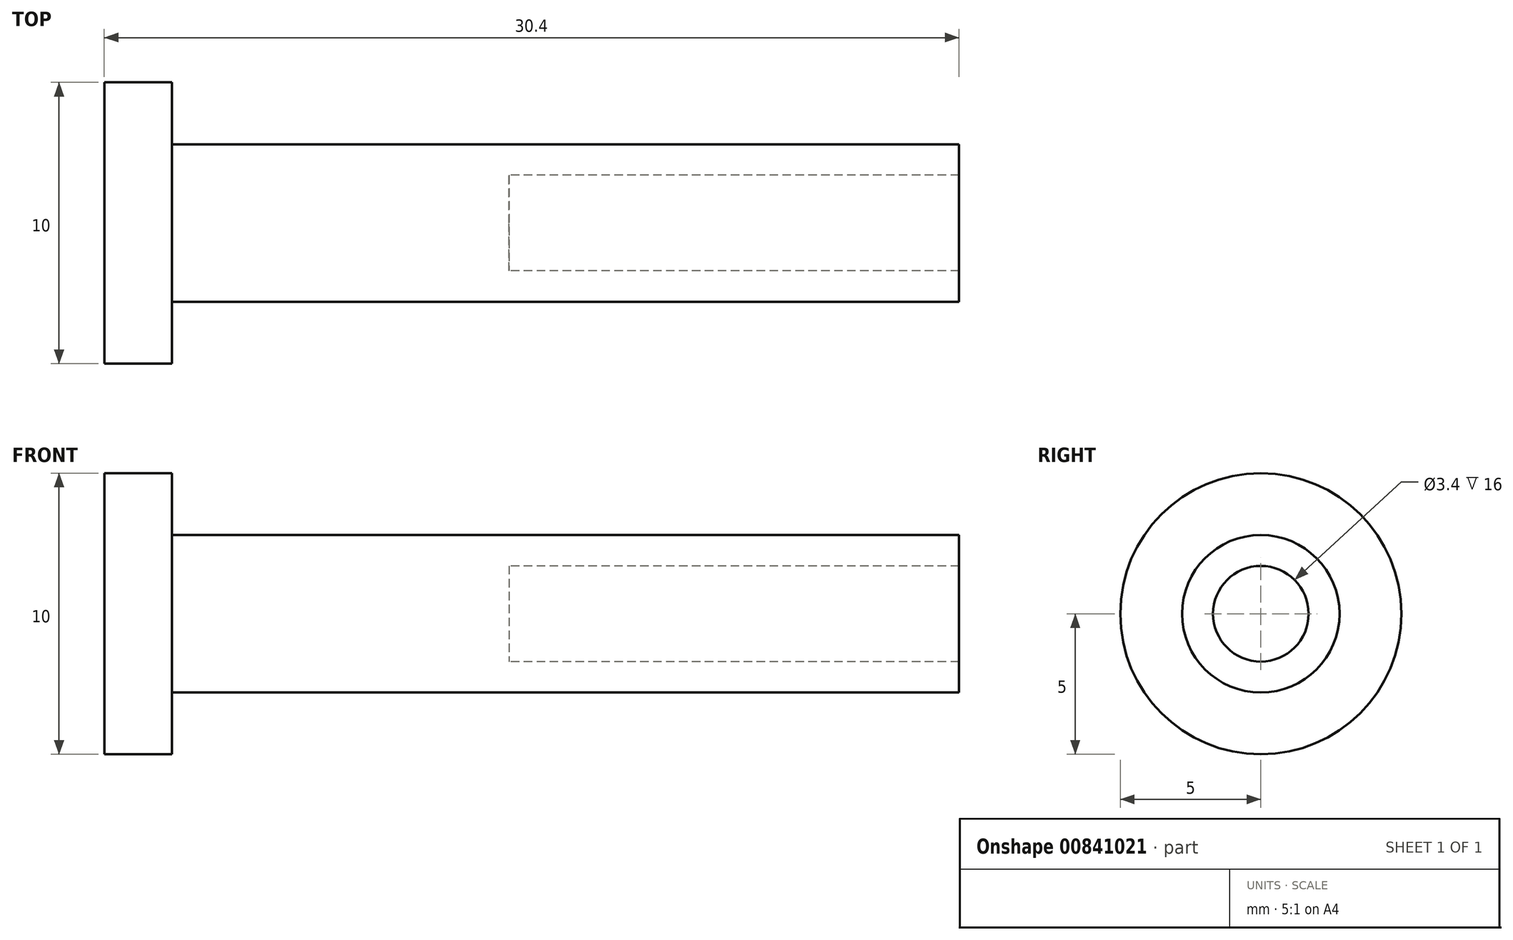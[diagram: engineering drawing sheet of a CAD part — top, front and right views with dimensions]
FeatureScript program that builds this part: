
annotation { "Feature Type Name" : "Feature", "Feature Type Description" : "" }
export const myFeature = defineFeature(function(context is Context, id is Id, definition is map)
    precondition{}
    {
        {
            var Q0;
            Q0=qCreatedBy(makeId("Front.planeOp"),FACE);
            var sketch = newSketch(context, id + "F0", { "sketchPlane" : qUnion([Q0])});
            skLineSegment(sketch, "E0", {"start": v(-11.46, 0) * mm, "end": v(2.94, 0) * mm});
            skLineSegment(sketch, "E1", {"start": v(18.94, 1.7) * mm, "end": v(18.94, 2.8) * mm});
            skLineSegment(sketch, "E2", {"start": v(18.94, 2.8) * mm, "end": v(-9.06, 2.8) * mm});
            skLineSegment(sketch, "E3", {"start": v(-9.06, 2.8) * mm, "end": v(-9.06, 5) * mm});
            skLineSegment(sketch, "E4", {"start": v(-9.06, 5) * mm, "end": v(-11.46, 5) * mm});
            skLineSegment(sketch, "E5", {"start": v(-11.46, 0) * mm, "end": v(-11.46, 5) * mm});
            skLineSegment(sketch, "E6", {"start": v(18.94, 1.7) * mm, "end": v(2.94, 1.7) * mm});
            skLineSegment(sketch, "E7", {"start": v(2.94, 1.7) * mm, "end": v(2.94, 0) * mm});
            skSolve(sketch);
        }
        {
            var Q0;
            Q0=makeQuery(id+"F0.imprint","IMPRINT",FACE,{"disambiguationData":[TD([[makeQuery(id+"F0.imprint","IMPRINT",EDGE,{"derivedFrom":sQuery(id+"F0.wireOp",EDGE,"E0")}),1.0]])]});
            var Q1;
            Q1=sQuery(id+"F0.wireOp",EDGE,"E0");
            revolve(context, id + "F1", {"surfaceOperationType" : NewSurfaceOperationType.NEW, "entities" : qUnion([Q0]), "axis" : qUnion([Q1]), "revolveType" : RevolveType.FULL});
        }
    });
